# Revit family: Plum Fix_Toilet_Argent_Vista Comfort High BTW S&P Trap UNI ENTRY
name_source: partatom
category: Plumbing Fixtures
revit_build: Autodesk Revit 2016 (Build: 20150220_1215(x64)
units: mm (PartAtom-declared; Revit-internal decimal feet)

## family parameters
Always vertical = Yes
Cut with Voids When Loaded = No
OmniClass Number = 23.45.05.21.11
OmniClass Title = Water Closets
Part Type = Normal
Room Calculation Point = No
Round Connector Dimension = Use Diameter
Shared = No
Work Plane-Based = No

## types (4) — shared parameters
Body Material = z_Argent_Ceramic White
CW Connection = Yes
Description = Vista Hygenic Flush Back-To-Wall Toilet Suite WELS 4 STAR/ 4.5/3L
Flush Material = z_Argent_Stainless Steel
HW Connection = No
Manufacturer = Argent
Manufacturer_Overall Depth = 635 mm
Manufacturer_Overall Height = 865 mm  [stored 2.83793 ft]
Manufacturer_Overall Width = 385 mm  [stored 1.26312 ft]
Manufacturer_Spec Code = 809911S4UB
Manufacturer_URL__Product Specific = https://www.argentaust.com.au
Model = 809911S4UB
ModifiedIssue_ANZRS = 20190503 $
Open Toilet Seat Visibility = No
Toilet Seat Visibility = Yes
Trap Offset = 170 mm
Trap Offset Value = 170 mm
URL = https://www.argentaust.com.au
Vent Connection = No
Waste Connection = Yes
zero-valued in all types: CWFU, Cost, HWFU, WFU

## per-type parameters (varying)
| type | Angle Offset | Toilet P Trap | Toilet S Trap | Trap Angle | Type Comments |
| S-Trap  - Rear Water Entry | 180 mm  [stored 0.590551 ft] | No | Yes | 90.00° | S-Trap - Rear Water Entry |
| P-Trap - Bottom Water Entry | 0 mm  [stored 0 ft] | Yes | No | 0.00° | P-Trap - Bottom Water Entry |
| P-Trap - Rear Water Entry | 180 mm  [stored 0.590551 ft] | Yes | No | 90.00° | P-Trap - Rear Water Entry |
| S-Trap - Bottom Water Entry | 0 mm  [stored 0 ft] | No | Yes | 0.00° | S-Trap - Bottom Water Entry |

note: [stored X ft] marks values corroborated as IEEE doubles in the binary element streams (Revit-internal decimal feet)

## geometry (parser evidence)
native form markers: Sweep x5
no freeform markers — native parametric forms only
